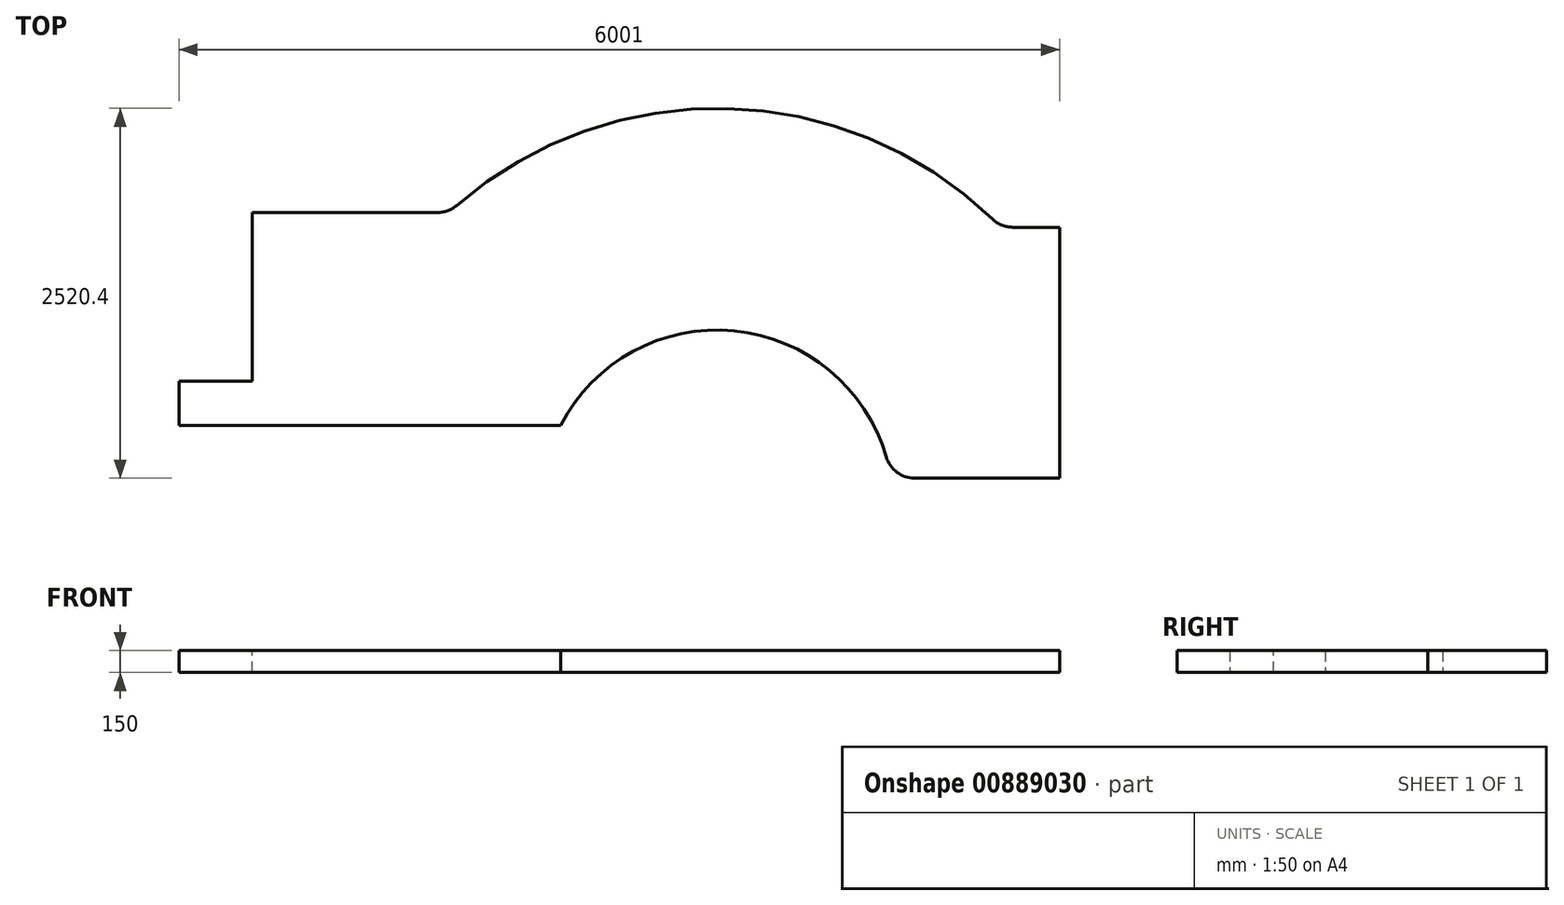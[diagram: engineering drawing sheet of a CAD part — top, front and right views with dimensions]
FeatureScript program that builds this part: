
annotation { "Feature Type Name" : "Feature", "Feature Type Description" : "" }
export const myFeature = defineFeature(function(context is Context, id is Id, definition is map)
    precondition{}
    {
        {
            var Q0;
            Q0=qCreatedBy(makeId("Top.planeOp"),FACE);
            var sketch = newSketch(context, id + "F0", { "sketchPlane" : qUnion([Q0])});
            skLineSegment(sketch, "E0", {"start": v(0, 0) * mm, "end": v(2100.5, 0) * mm});
            skLineSegment(sketch, "E1", {"start": v(0, 0) * mm, "end": v(0, 1450) * mm});
            skLineSegment(sketch, "E2", {"start": v(0, 1450) * mm, "end": v(1261.6, 1450) * mm});
            skArc(sketch, "E3", {"start": v(4320.23, -215.77) * mm, "mid": v(3283.49, 644.37) * mm, "end": v(2100.5, 0) * mm});
            skLineSegment(sketch, "E4", {"start": v(4512.3, -360) * mm, "end": v(5500.5, -360) * mm});
            skArc(sketch, "E5", {"start": v(5044.14, 1405.68) * mm, "mid": v(3236.55, 2159.52) * mm, "end": v(1392.84, 1498.92) * mm});
            skLineSegment(sketch, "E6", {"start": v(5182.6, 1350) * mm, "end": v(5500.5, 1350) * mm});
            skLineSegment(sketch, "E7", {"start": v(5500.5, 1350) * mm, "end": v(5500.5, -360) * mm});
            skPoint(sketch, "E8.visualSharp", {"position": v(1337.86, 1450) * mm});
            skArc(sketch, "E8.filletArc", {"start": v(1261.6, 1450) * mm, "mid": v(1331.63, 1462.63) * mm, "end": v(1392.84, 1498.92) * mm});
            skPoint(sketch, "E9.visualSharp", {"position": v(5100.5, 1350) * mm});
            skArc(sketch, "E9.filletArc", {"start": v(5044.14, 1405.68) * mm, "mid": v(5107.98, 1364.44) * mm, "end": v(5182.6, 1350) * mm});
            skPoint(sketch, "E10.visualSharp", {"position": v(4352.63, -360) * mm});
            skArc(sketch, "E10.filletArc", {"start": v(4320.23, -215.77) * mm, "mid": v(4392.2, -319.93) * mm, "end": v(4512.3, -360) * mm});
            skPoint(sketch, "E11.visualSharp", {"position": v(2100.5, 0) * mm});
            skSolve(sketch);
        }
        {
            var Q0;
            Q0 = qSketchRegion(id + "F0", true);
            extrude(context, id + "F1", {"entities" : qUnion([Q0]), "depth" : 150 * mm, "offsetDistance" : 25 * mm});
        }
        {
            var Q0;
            Q0=makeQuery(id+"F1.opExtrude","CAP_FACE",FACE,{"disambiguationData":[OSD([sQuery(id+"F0.wireOp",EDGE,"E0"),sQuery(id+"F0.wireOp",EDGE,"E1"),sQuery(id+"F0.wireOp",EDGE,"E2"),sQuery(id+"F0.wireOp",EDGE,"E3"),sQuery(id+"F0.wireOp",EDGE,"E4"),sQuery(id+"F0.wireOp",EDGE,"E5"),sQuery(id+"F0.wireOp",EDGE,"E6"),sQuery(id+"F0.wireOp",EDGE,"E7"),sQuery(id+"F0.wireOp",EDGE,"E8.filletArc"),sQuery(id+"F0.wireOp",EDGE,"E9.filletArc"),sQuery(id+"F0.wireOp",EDGE,"E10.filletArc"),sQuery(id+"F0.wireOp",EDGE,"E11.filletArc")])],"isStart":false});
            var sketch = newSketch(context, id + "F2", { "sketchPlane" : qUnion([Q0])});
            skLineSegment(sketch, "E12.bottom", {"start": v(0, 0) * mm, "end": v(-500.5, 0) * mm});
            skLineSegment(sketch, "E12.top", {"start": v(0, 300) * mm, "end": v(-500.5, 300) * mm});
            skLineSegment(sketch, "E12.left", {"start": v(0, 0) * mm, "end": v(0, 300) * mm});
            skLineSegment(sketch, "E12.right", {"start": v(-500.5, 0) * mm, "end": v(-500.5, 300) * mm});
            skSolve(sketch);
        }
        {
            var Q0;
            Q0 = qSketchRegion(id + "F2", true);
            var Q1;
            Q1=makeQuery(id+"F1.opExtrude","CAP_FACE",FACE,{"disambiguationData":[OSD([sQuery(id+"F0.wireOp",EDGE,"E0"),sQuery(id+"F0.wireOp",EDGE,"E1"),sQuery(id+"F0.wireOp",EDGE,"E2"),sQuery(id+"F0.wireOp",EDGE,"E3"),sQuery(id+"F0.wireOp",EDGE,"E4"),sQuery(id+"F0.wireOp",EDGE,"E5"),sQuery(id+"F0.wireOp",EDGE,"E6"),sQuery(id+"F0.wireOp",EDGE,"E7"),sQuery(id+"F0.wireOp",EDGE,"E8.filletArc"),sQuery(id+"F0.wireOp",EDGE,"E9.filletArc"),sQuery(id+"F0.wireOp",EDGE,"E10.filletArc"),sQuery(id+"F0.wireOp",EDGE,"E11.filletArc")])],"isStart":true});
            extrude(context, id + "F3", {"entities" : qUnion([Q0]), "operationType" : NewBodyOperationType.ADD, "endBound" : BoundingType.UP_TO_SURFACE, "oppositeDirection" : true, "depth" : 25 * mm, "endBoundEntityFace" : qUnion([Q1]), "offsetDistance" : 25 * mm});
        }
    });
